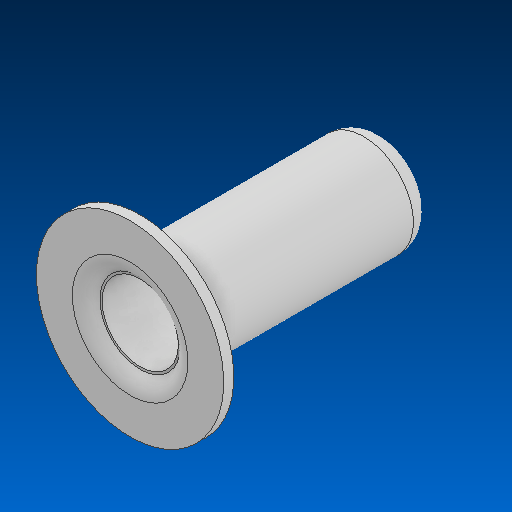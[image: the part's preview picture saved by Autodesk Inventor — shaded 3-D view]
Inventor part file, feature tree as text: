
AUTODESK INVENTOR PART (.ipt)
format: ipt  version: 2022.2 (Build 262287000, 287)  size: 129,536 bytes
history: native  units: in
note: dims shown in document units (in); Inventor stores cm internally (conversion verified against a paired STEP export)
features: fillet x1
ambient origin geometry x8: Origin, YZ Plane, XZ Plane, XY Plane, X Axis, Y Axis, Z Axis, Center Point
bodies: Solid1 (feature_tree)
feature tree (1):
  fillet  "Fillet1"  [1 undecoded]
note: 1 required parameter value undecoded (feature->parameter linkage not recoverable at this tier; creation-order binding heuristic only, values carry confidence <= 0.55)
